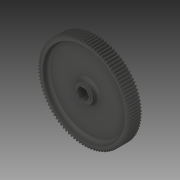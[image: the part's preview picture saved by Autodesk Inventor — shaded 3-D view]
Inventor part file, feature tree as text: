
AUTODESK INVENTOR PART (.ipt)
format: ipt  version: 2019 (Build 230136000, 136)  size: 999,936 bytes
history: native  units: in
note: dims shown in document units (in); Inventor stores cm internally (conversion verified against a paired STEP export)
features: mirror x1
ambient origin geometry x8: Origin, YZ Plane, XZ Plane, XY Plane, X Axis, Y Axis, Z Axis, Center Point
bodies: Solid1 (feature_tree)
feature tree (1):
  mirror  "Mirror1"
